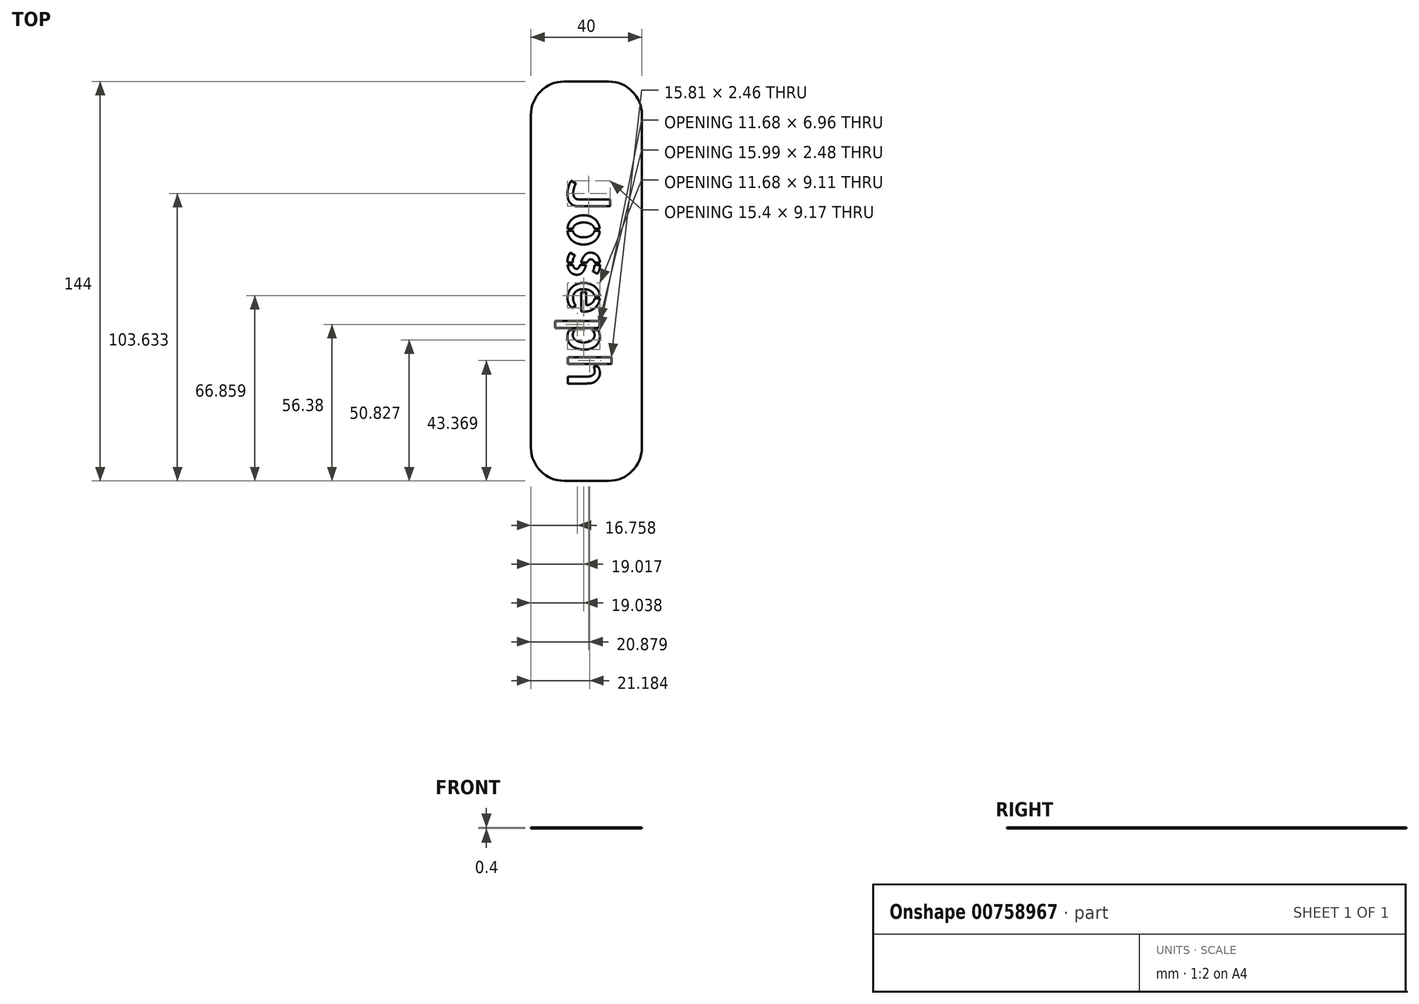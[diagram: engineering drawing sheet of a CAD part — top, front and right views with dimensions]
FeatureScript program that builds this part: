
annotation { "Feature Type Name" : "Feature", "Feature Type Description" : "" }
export const myFeature = defineFeature(function(context is Context, id is Id, definition is map)
    precondition{}
    {
        {
            var Q0;
            Q0=qCreatedBy(makeId("Top.planeOp"),FACE);
            var sketch = newSketch(context, id + "F0", { "sketchPlane" : qUnion([Q0])});
            skLineSegment(sketch, "E0.bottom", {"start": v(0, 0) * mm, "end": v(40, 0) * mm});
            skLineSegment(sketch, "E0.top", {"start": v(0, 144) * mm, "end": v(40, 144) * mm});
            skLineSegment(sketch, "E0.left", {"start": v(0, 0) * mm, "end": v(0, 144) * mm});
            skLineSegment(sketch, "E0.right", {"start": v(40, 0) * mm, "end": v(40, 144) * mm});
            skSolve(sketch);
        }
        {
            var Q0;
            Q0=makeQuery(id+"F0.imprint","IMPRINT",FACE,{"disambiguationData":[TD([[makeQuery(id+"F0.imprint","IMPRINT",EDGE,{"derivedFrom":sQuery(id+"F0.wireOp",EDGE,"E0.bottom")}),1.0]])]});
            extrude(context, id + "F1", {"entities" : qUnion([Q0]), "depth" : .4 * mm, "offsetDistance" : 25 * mm});
        }
        {
            var Q0;
            Q0=makeQuery(id+"F1.opExtrude","SWEPT_EDGE",EDGE,{"disambiguationData":[OSD([sQuery(id+"F0.wireOp",EDGE,"E0.top"),sQuery(id+"F0.wireOp",EDGE,"E0.left")])]});
            var Q1;
            Q1=makeQuery(id+"F1.opExtrude","SWEPT_EDGE",EDGE,{"disambiguationData":[OSD([sQuery(id+"F0.wireOp",EDGE,"E0.top"),sQuery(id+"F0.wireOp",EDGE,"E0.right")])]});
            var Q2;
            Q2=makeQuery(id+"F1.opExtrude","SWEPT_EDGE",EDGE,{"disambiguationData":[OSD([sQuery(id+"F0.wireOp",EDGE,"E0.bottom"),sQuery(id+"F0.wireOp",EDGE,"E0.right")])]});
            var Q3;
            Q3=makeQuery(id+"F1.opExtrude","SWEPT_EDGE",EDGE,{"disambiguationData":[OSD([sQuery(id+"F0.wireOp",EDGE,"E0.bottom"),sQuery(id+"F0.wireOp",EDGE,"E0.left")])]});
            fillet(context, id + "F2", {"entities" : qUnion([Q0, Q1, Q2, Q3]), "radius" : 12 * mm, "tangentPropagation" : true, "allowEdgeOverflow" : false});
        }
        {
            var Q0;
            Q0=makeQuery(id+"F1.opExtrude","CAP_FACE",FACE,{"disambiguationData":[OSD([sQuery(id+"F0.wireOp",EDGE,"E0.bottom"),sQuery(id+"F0.wireOp",EDGE,"E0.top"),sQuery(id+"F0.wireOp",EDGE,"E0.left"),sQuery(id+"F0.wireOp",EDGE,"E0.right")])],"isStart":false});
            var sketch = newSketch(context, id + "F3", { "sketchPlane" : qUnion([Q0])});
            skText(sketch, "E1", { "text": "Joseph", "fontName": "AllertaStencil-Regular.ttf"});
            const initialGuessF3  = {"E1": [0.01328, 0.10875, 0, -1, 0.015]};
            skSetInitialGuess(sketch, initialGuessF3);
            skSolve(sketch);
        }
        {
            var Q0;
            Q0=qSketchRegion(id+"F3",true);
            extrude(context, id + "F4", {"entities" : qUnion([Q0]), "operationType" : NewBodyOperationType.REMOVE, "endBound" : BoundingType.THROUGH_ALL, "oppositeDirection" : true, "depth" : 25 * mm, "offsetDistance" : 25 * mm});
        }
    });
